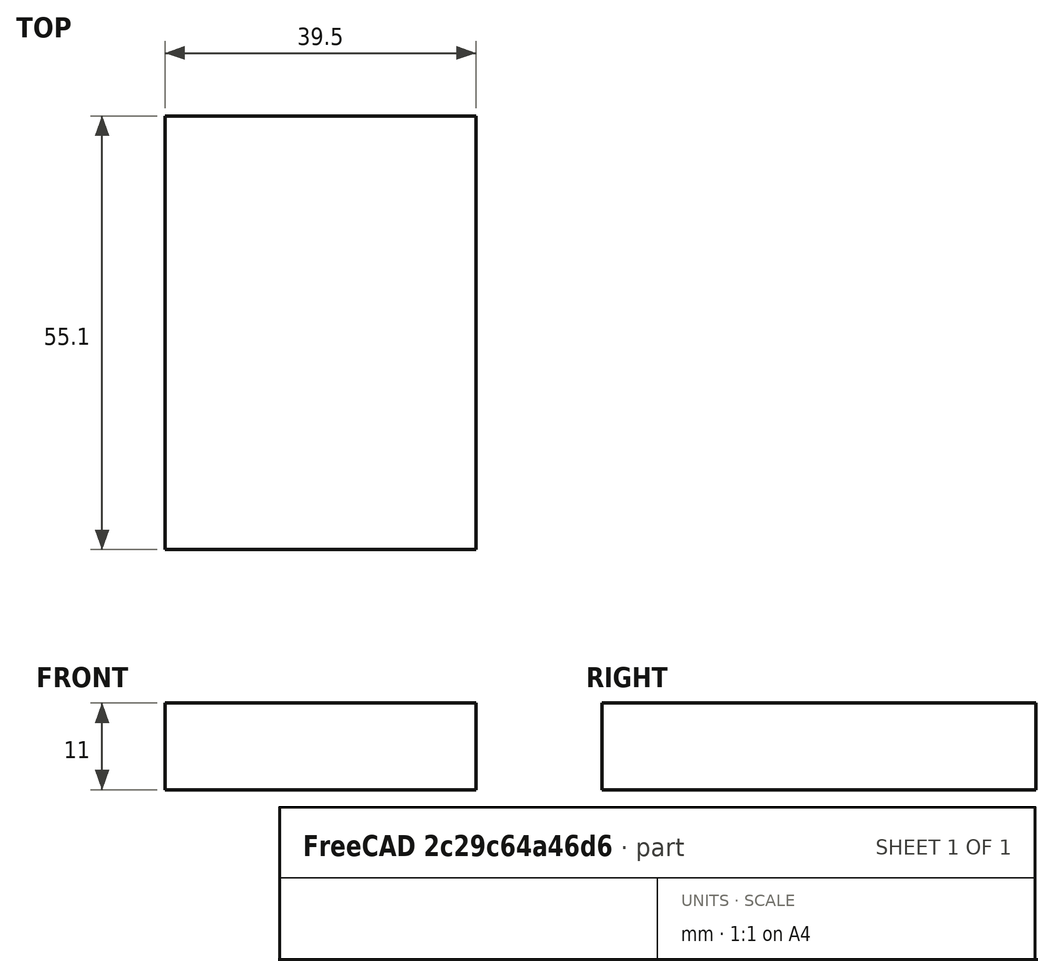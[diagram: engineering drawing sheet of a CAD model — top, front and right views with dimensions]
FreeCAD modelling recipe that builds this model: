
FCSTD DOCUMENT  (FreeCAD 0.20R29410 (Git))
Label: electronics
License: All rights reserved
LicenseURL: http://en.wikipedia.org/wiki/All_rights_reserved
objects: Sketcher::SketchObject×1, PartDesign::Pad×1, PartDesign::Body×1, App::Link×1
note: 4 computed .brp shape members not serialized (recipe doc carries the construction recipe); baked Part::Feature solids carry a one-line shape summary decoded from their .brp

FEATURE [Sketcher::SketchObject] Sketch
  FullyConstrained = true
  MapMode = 5
  Support = -> [XY_Plane]
  sketch-geometry (4):
    g0: LineSegment StartX=-19.75 StartY=27.55 StartZ=0 EndX=19.75 EndY=27.55 EndZ=0
    g1: LineSegment StartX=19.75 StartY=27.55 StartZ=0 EndX=19.75 EndY=-27.55 EndZ=0
    g2: LineSegment StartX=19.75 StartY=-27.55 StartZ=0 EndX=-19.75 EndY=-27.55 EndZ=0
    g3: LineSegment StartX=-19.75 StartY=-27.55 StartZ=0 EndX=-19.75 EndY=27.55 EndZ=0
  constraints (10):
    c: Coincident(g0,g1)
    c: Coincident(g1,g2)
    c: Coincident(g2,g3)
    c: Coincident(g3,g0)
    c: Horizontal(g2)
    c: Vertical(g1)
    c: DistanceY(g1,g1) = 55.1
    c: DistanceX(g0,g0) = 39.5
    c: Symmetric(g0,g0,g-2)
    c: Symmetric(g2,g0,g-1)
FEATURE [PartDesign::Pad] Pad  label="pad"
  Direction = (0,0,1)
  Length = 11
  Length2 = 10
  Profile = -> Sketch
  ReferenceAxis = -> Sketch [N_Axis]
  Type = 0
FEATURE [PartDesign::Body] Body  label="electronics"
  Group = -> [Sketch,Pad]
  Origin = -> Origin
  Tip = -> Pad
FEATURE [App::Link] Link  label="electronics001"
  LinkedObject = -> Body
